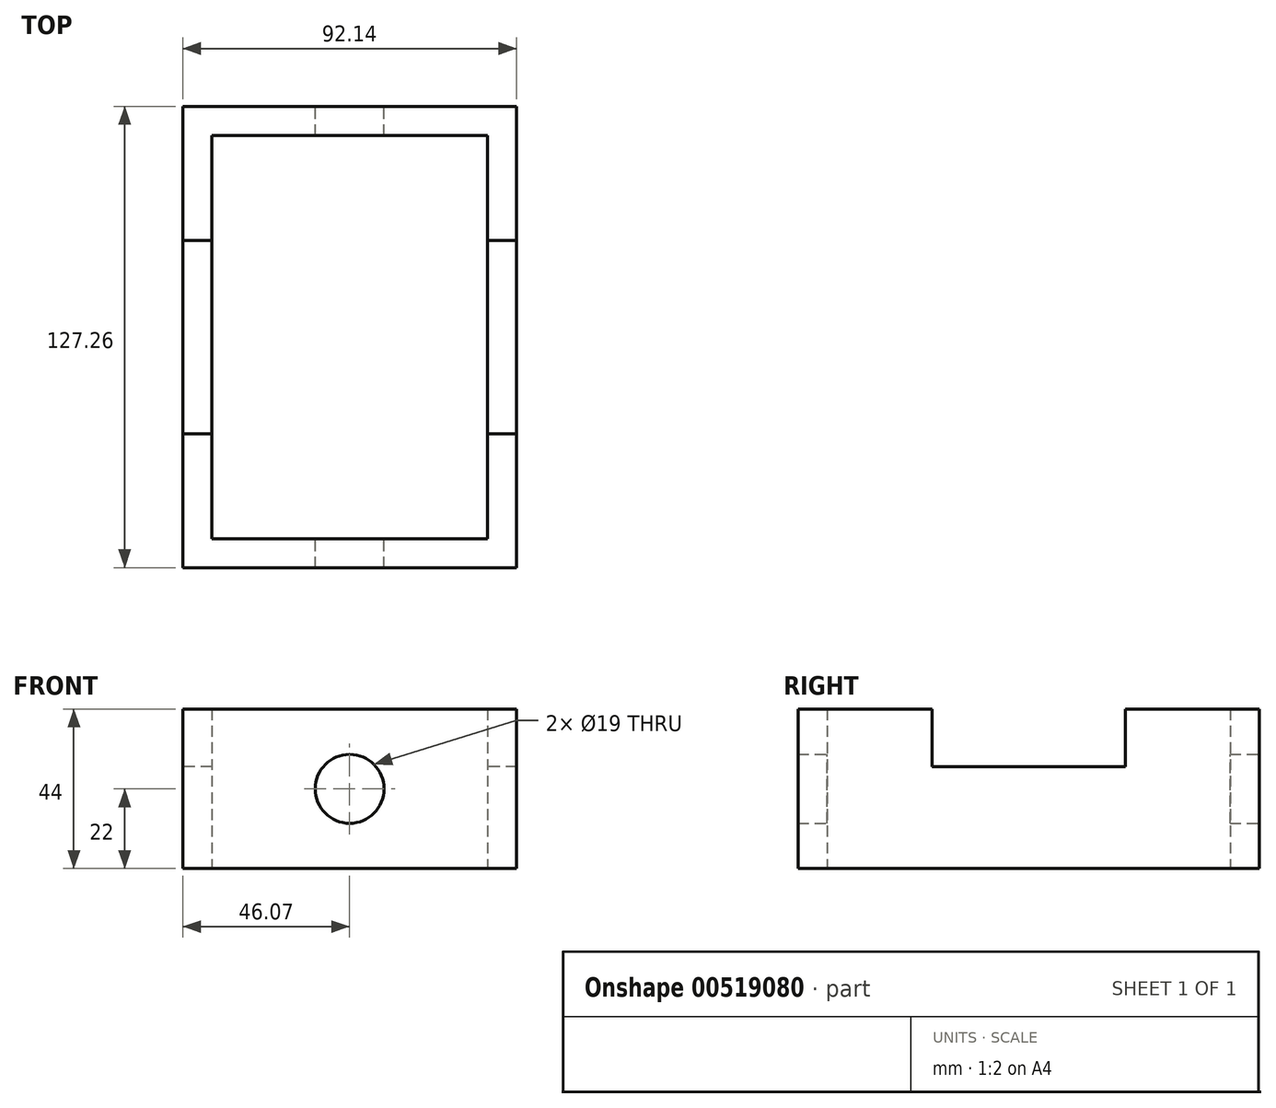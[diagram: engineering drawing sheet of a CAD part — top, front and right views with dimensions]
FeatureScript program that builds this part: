
annotation { "Feature Type Name" : "Feature", "Feature Type Description" : "" }
export const myFeature = defineFeature(function(context is Context, id is Id, definition is map)
    precondition{}
    {
        {
            var Q0;
            Q0=qCreatedBy(makeId("Top.planeOp"),FACE);
            var sketch = newSketch(context, id + "F0", { "sketchPlane" : qUnion([Q0])});
            skLineSegment(sketch, "E0.bottom", {"start": v(46.07, 63.63) * mm, "end": v(-46.07, 63.63) * mm});
            skLineSegment(sketch, "E0.top", {"start": v(46.07, -63.63) * mm, "end": v(-46.07, -63.63) * mm});
            skLineSegment(sketch, "E0.left", {"start": v(46.07, 63.63) * mm, "end": v(46.07, -63.63) * mm});
            skLineSegment(sketch, "E0.right", {"start": v(-46.07, 63.63) * mm, "end": v(-46.07, -63.63) * mm});
            skPoint(sketch, "E0.middle", {"position": v(0, 0) * mm});
            skLineSegment(sketch, "E1.0", {"start": v(38.07, 55.63) * mm, "end": v(-38.07, 55.63) * mm});
            skLineSegment(sketch, "E1.1", {"start": v(38.07, 55.63) * mm, "end": v(38.07, -55.63) * mm});
            skLineSegment(sketch, "E1.2", {"start": v(38.07, -55.63) * mm, "end": v(-38.07, -55.63) * mm});
            skLineSegment(sketch, "E1.3", {"start": v(-38.07, 55.63) * mm, "end": v(-38.07, -55.63) * mm});
            skSolve(sketch);
        }
        {
            var Q0;
            Q0=makeQuery(id+"F0.imprint","IMPRINT",FACE,{"disambiguationData":[TD([[makeQuery(id+"F0.imprint","IMPRINT",EDGE,{"derivedFrom":sQuery(id+"F0.wireOp",EDGE,"E0.bottom")}),1.0]])]});
            extrude(context, id + "F1", {"entities" : qUnion([Q0]), "depth" : 44 * mm, "offsetDistance" : 25 * mm});
        }
        {
            var Q0;
            Q0=makeQuery(id+"F1.opExtrude","SWEPT_FACE",FACE,{"disambiguationData":[OSD([sQuery(id+"F0.wireOp",EDGE,"E0.left")])]});
            var sketch = newSketch(context, id + "F2", { "sketchPlane" : qUnion([Q0])});
            skLineSegment(sketch, "E2.bottom", {"start": v(26.7, 28.08) * mm, "end": v(-26.7, 28.08) * mm});
            skLineSegment(sketch, "E2.top", {"start": v(26.7, 59.92) * mm, "end": v(-26.7, 59.92) * mm});
            skLineSegment(sketch, "E2.left", {"start": v(26.7, 28.08) * mm, "end": v(26.7, 59.92) * mm});
            skLineSegment(sketch, "E2.right", {"start": v(-26.7, 28.08) * mm, "end": v(-26.7, 59.92) * mm});
            skPoint(sketch, "E2.middle", {"position": v(0, 44) * mm});
            skLineSegment(sketch, "E3.bottom", {"start": v(-26.7, 28.08) * mm, "end": v(26.7, 28.08) * mm});
            skLineSegment(sketch, "E3.top", {"start": v(-26.7, 59.92) * mm, "end": v(26.7, 59.92) * mm});
            skSolve(sketch);
        }
        {
            var Q0;
            Q0=makeQuery(id+"F1.opExtrude","SWEPT_FACE",FACE,{"disambiguationData":[OSD([sQuery(id+"F0.wireOp",EDGE,"E0.right")])]});
            var sketch = newSketch(context, id + "F3", { "sketchPlane" : qUnion([Q0])});
            skLineSegment(sketch, "E4.bottom", {"start": v(26.7, 28.08) * mm, "end": v(-26.7, 28.08) * mm});
            skLineSegment(sketch, "E4.top", {"start": v(26.7, 59.92) * mm, "end": v(-26.7, 59.92) * mm});
            skLineSegment(sketch, "E4.left", {"start": v(26.7, 28.08) * mm, "end": v(26.7, 59.92) * mm});
            skLineSegment(sketch, "E4.right", {"start": v(-26.7, 28.08) * mm, "end": v(-26.7, 59.92) * mm});
            skPoint(sketch, "E4.middle", {"position": v(0, 44) * mm});
            skSolve(sketch);
        }
        {
            var Q0;
            {var subQ0=sQuery(id+"F3.wireOp",EDGE,"E4.bottom");Q0=makeQuery(id+"F3.imprint","IMPRINT",FACE,{"disambiguationData":[TD([[makeQuery(id+"F3.imprint","IMPRINT",EDGE,{"derivedFrom":subQ0}),-1.0]])]});}
            var Q1;
            {var subQ0=sQuery(id+"F2.wireOp",EDGE,"E3.bottom");Q1=makeQuery(id+"F2.imprint","IMPRINT",FACE,{"disambiguationData":[TD([[makeQuery(id+"F2.imprint","IMPRINT",EDGE,{"derivedFrom":subQ0}),1.0]])]});}
            extrude(context, id + "F4", {"entities" : qUnion([Q0, Q1]), "operationType" : NewBodyOperationType.REMOVE, "oppositeDirection" : true, "depth" : 146.8 * mm, "offsetDistance" : 25 * mm});
        }
        {
            var Q0;
            Q0=makeQuery(id+"F1.opExtrude","SWEPT_FACE",FACE,{"disambiguationData":[OSD([sQuery(id+"F0.wireOp",EDGE,"E0.top")])]});
            var sketch = newSketch(context, id + "F5", { "sketchPlane" : qUnion([Q0])});
            skCircle(sketch, "E5", {"center": v(0, 22) * mm, "radius": 9.5 * mm});
            skPoint(sketch, "E5.centerSnap0", {"position": v(46.07, 22) * mm});
            skSolve(sketch);
        }
        {
            var Q0;
            Q0=makeQuery(id+"F1.opExtrude","SWEPT_FACE",FACE,{"disambiguationData":[OSD([sQuery(id+"F0.wireOp",EDGE,"E0.bottom")])]});
            var sketch = newSketch(context, id + "F6", { "sketchPlane" : qUnion([Q0])});
            skCircle(sketch, "E6", {"center": v(0, 22) * mm, "radius": 9.5 * mm});
            skPoint(sketch, "E6.centerSnap0", {"position": v(-46.07, 22) * mm});
            skSolve(sketch);
        }
        {
            var Q0;
            Q0=makeQuery(id+"F6.imprint","IMPRINT",FACE,{"disambiguationData":[TD([[makeQuery(id+"F6.imprint","IMPRINT",EDGE,{"derivedFrom":sQuery(id+"F6.wireOp",EDGE,"E6")}),1.0]])]});
            var Q1;
            Q1=makeQuery(id+"F5.imprint","IMPRINT",FACE,{"disambiguationData":[TD([[makeQuery(id+"F5.imprint","IMPRINT",EDGE,{"derivedFrom":sQuery(id+"F5.wireOp",EDGE,"E5")}),1.0]])]});
            extrude(context, id + "F7", {"entities" : qUnion([Q0, Q1]), "operationType" : NewBodyOperationType.REMOVE, "oppositeDirection" : true, "depth" : 171.1 * mm, "offsetDistance" : 25 * mm});
        }
    });
